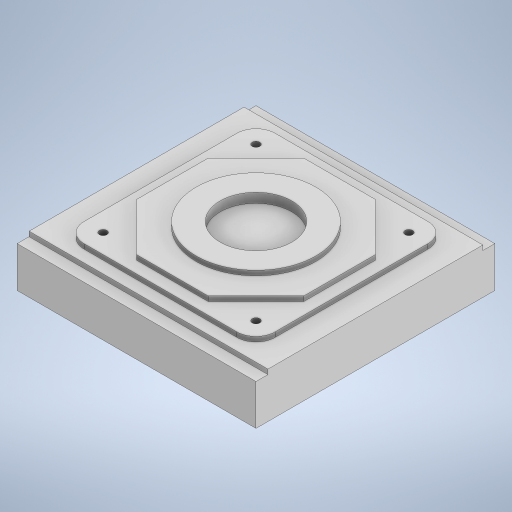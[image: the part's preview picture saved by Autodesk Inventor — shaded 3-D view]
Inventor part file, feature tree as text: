
AUTODESK INVENTOR PART (.ipt)
format: ipt  version: 2023.2 (Build 272271000, 271)  size: 322,048 bytes
history: native  units: mm
features: sketch x7, extrude x6, hole x1
ambient origin geometry x8: Origin, YZ Plane, XZ Plane, XY Plane, X Axis, Y Axis, Z Axis, Center Point
bodies: Solid1 (feature_tree)
feature tree (14):
  extrude  "Extrusion1"  Depth=100.0mm
  extrude  "Extrusion2"  Depth=5.0mm
  extrude  "Extrusion3"  Depth=2.0mm TaperAngle=0.0deg
  extrude  "Extrusion4"  Depth=80.0mm
  extrude  "Extrusion5"  Depth=2.0mm TaperAngle=0.0deg
  extrude  "Extrusion6"  Depth=85.0mm
  hole  "Hole2"  [1 undecoded]
  sketch  "Sketch1"  dims[d0=100.0mm d1=100.0mm]
  sketch  "Sketch2"  dims[d2=17.0mm d3=0.0mm d4=5.0mm]
  sketch  "Sketch3"  dims[d5=5.0mm d6=2.0mm d7=0.0mm]
  sketch  "Sketch4"  dims[d8=80.0mm d9=80.0mm]
  sketch  "Sketch5"  dims[d10=8.0mm d11=2.0mm d12=0.0mm]
  sketch  "Sketch6"  dims[d13=85.0mm d14=65.0mm]
  sketch  "Sketch7"  dims[d15=65.0mm d16=85.0mm d17=2.0mm d18=0.0mm d19=50.0mm d20=2.0mm d21=0.0mm d22=30.0mm d23=4.0mm d24=0.0mm d25=3.0mm d26=18.0mm d27=18.0mm d28=20.0mm d30=64.0mm d31=20.0mm d33=64.0mm d43=3.121114mm d44=8.0mm d45=4.0mm d46=2.0mm d47=90.0deg d48=9.1mm d49=20.594885mm]
note: 1 required parameter value undecoded (feature->parameter linkage not recoverable at this tier; creation-order binding heuristic only, values carry confidence <= 0.55)
